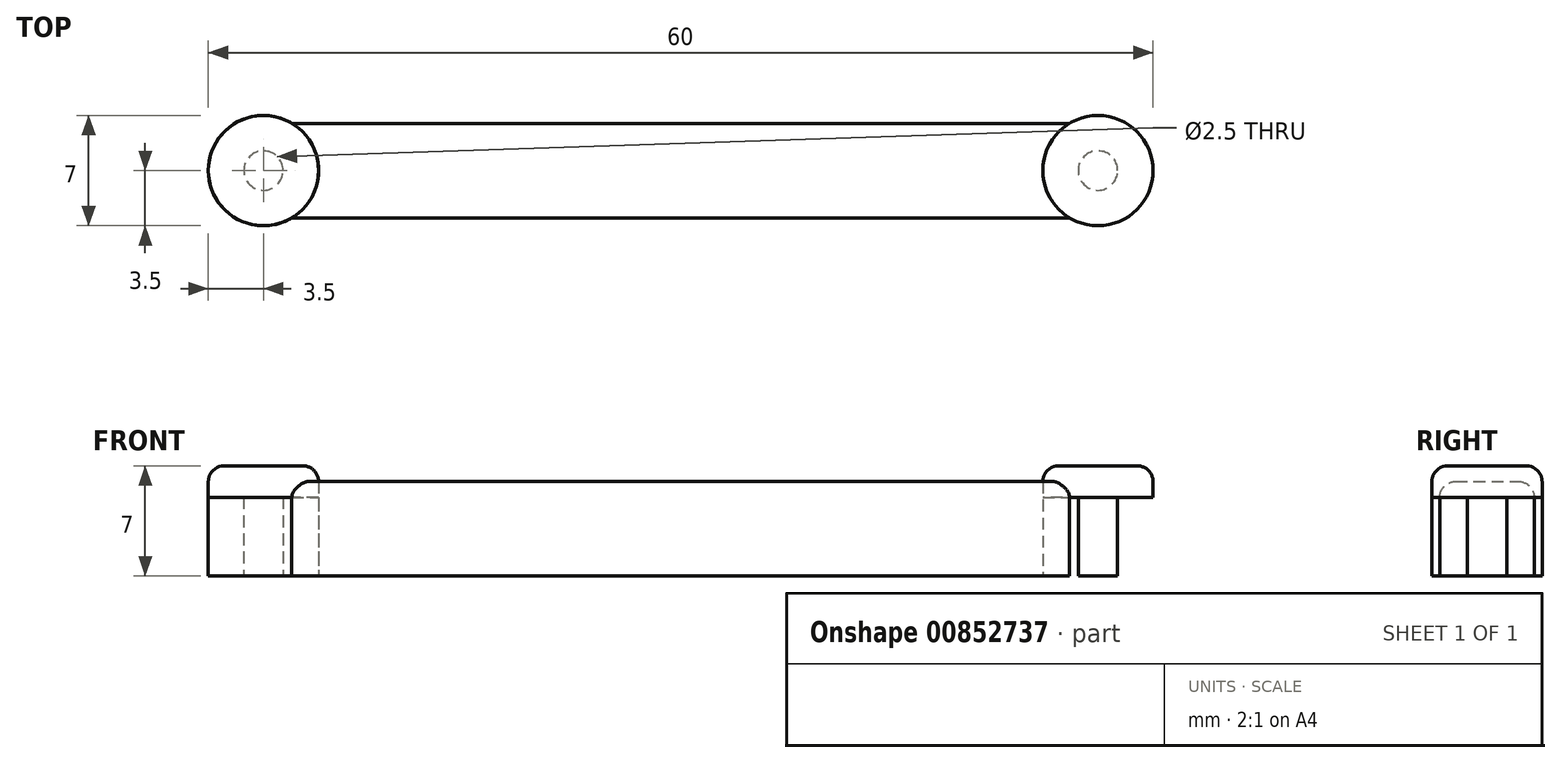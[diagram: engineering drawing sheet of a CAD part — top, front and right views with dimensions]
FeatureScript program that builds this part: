
annotation { "Feature Type Name" : "Feature", "Feature Type Description" : "" }
export const myFeature = defineFeature(function(context is Context, id is Id, definition is map)
    precondition{}
    {
        {
            var Q0;
            Q0=qCreatedBy(makeId("Top.planeOp"),FACE);
            var sketch = newSketch(context, id + "F0", { "sketchPlane" : qUnion([Q0])});
            skLineSegment(sketch, "E0", {"start": v(-26.5, 0) * mm, "end": v(26.5, 0) * mm, "construction": true});
            skCircle(sketch, "E1", {"center": v(-26.5, 0) * mm, "radius": 3.5 * mm});
            skCircle(sketch, "E2", {"center": v(26.5, 0) * mm, "radius": 3.5 * mm});
            skLineSegment(sketch, "E3", {"start": v(-24.7, 3) * mm, "end": v(24.7, 3) * mm});
            skLineSegment(sketch, "E4.MirrorCS", {"start": v(-24.7, -3) * mm, "end": v(24.7, -3) * mm});
            skCircle(sketch, "E5", {"center": v(-26.5, 0) * mm, "radius": 1.25 * mm});
            skCircle(sketch, "E6.MirrorC", {"center": v(26.5, 0) * mm, "radius": 1.25 * mm});
            skSolve(sketch);
        }
        {
            var Q0;
            Q0=makeQuery(id+"F0.imprint","IMPRINT",FACE,{"disambiguationData":[TD([[makeQuery(id+"F0.imprint","IMPRINT",EDGE,{"derivedFrom":sQuery(id+"F0.wireOp",EDGE,"E5")}),-1.0]])]});
            var Q1;
            Q1=makeQuery(id+"F0.imprint","IMPRINT",FACE,{"disambiguationData":[TD([[makeQuery(id+"F0.imprint","IMPRINT",EDGE,{"derivedFrom":sQuery(id+"F0.wireOp",EDGE,"E6.MirrorC")}),1.0]])]});
            extrude(context, id + "F1", {"entities" : qUnion([Q0, Q1]), "depth" : 5 * mm, "offsetDistance" : 25 * mm});
        }
        {
            var Q0;
            {var subQ0=sQuery(id+"F0.wireOp",EDGE,"E3");Q0=makeQuery(id+"F0.imprint","IMPRINT",FACE,{"disambiguationData":[TD([[makeQuery(id+"F0.imprint","IMPRINT",EDGE,{"derivedFrom":subQ0}),-1.0]])]});}
            extrude(context, id + "F2", {"entities" : qUnion([Q0]), "depth" : 6 * mm, "offsetDistance" : 25 * mm});
        }
        {
            var Q0;
            Q0=makeQuery(id+"F1.opExtrude","CAP_FACE",FACE,{"disambiguationData":[OSD([sQuery(id+"F0.wireOp",EDGE,"E1"),sQuery(id+"F0.wireOp",EDGE,"E5")])],"isStart":false});
            var sketch = newSketch(context, id + "F3", { "sketchPlane" : qUnion([Q0])});
            skCircle(sketch, "E7.0.0", {"center": v(-26.5, 0) * mm, "radius": 3.5 * mm});
            skSolve(sketch);
        }
        {
            var Q0;
            Q0 = qSketchRegion(id + "F3", true);
            extrude(context, id + "F4", {"entities" : qUnion([Q0]), "depth" : 2 * mm, "offsetDistance" : 25 * mm});
        }
        {
            var Q0;
            Q0=makeQuery(id+"F1.opExtrude","CAP_FACE",FACE,{"disambiguationData":[OSD([sQuery(id+"F0.wireOp",EDGE,"E2"),sQuery(id+"F0.wireOp",EDGE,"E6.MirrorC")])],"isStart":false});
            var sketch = newSketch(context, id + "F5", { "sketchPlane" : qUnion([Q0])});
            skCircle(sketch, "E8.0.0", {"center": v(26.5, 0) * mm, "radius": 3.5 * mm});
            skSolve(sketch);
        }
        {
            var Q0;
            Q0 = qSketchRegion(id + "F5", true);
            extrude(context, id + "F6", {"entities" : qUnion([Q0]), "depth" : 2 * mm, "offsetDistance" : 25 * mm});
        }
        {
            var Q0;
            Q0=makeQuery(id+"F2.opExtrude","CAP_EDGE",EDGE,{"disambiguationData":[OSD([sQuery(id+"F0.wireOp",EDGE,"E3")])],"isStart":false});
            var Q1;
            Q1=makeQuery(id+"F2.opExtrude","CAP_EDGE",EDGE,{"disambiguationData":[OSD([sQuery(id+"F0.wireOp",EDGE,"E4.MirrorCS")])],"isStart":false});
            var Q2;
            Q2=makeQuery(id+"F6.opExtrude","CAP_EDGE",EDGE,{"disambiguationData":[OSD([sQuery(id+"F5.wireOp",EDGE,"E8.0.0")])],"isStart":false});
            var Q3;
            Q3=makeQuery(id+"F4.opExtrude","CAP_EDGE",EDGE,{"disambiguationData":[OSD([sQuery(id+"F3.wireOp",EDGE,"E7.0.0")])],"isStart":false});
            fillet(context, id + "F7", {"entities" : qUnion([Q0, Q1, Q2, Q3]), "radius" : 1 * mm, "tangentPropagation" : true, "allowEdgeOverflow" : false});
        }
    });
